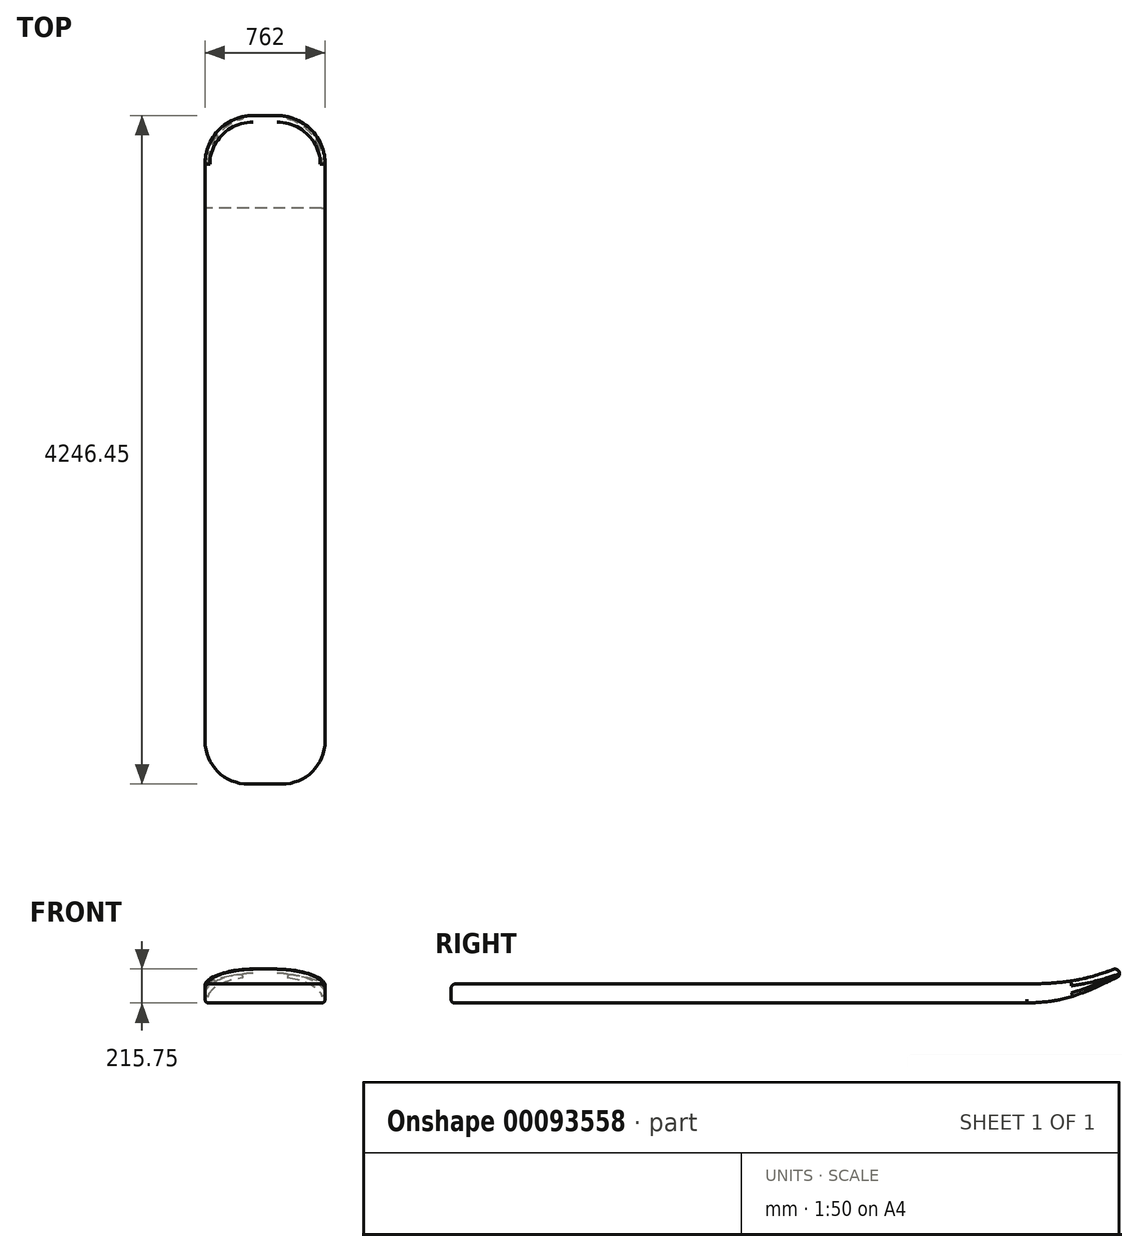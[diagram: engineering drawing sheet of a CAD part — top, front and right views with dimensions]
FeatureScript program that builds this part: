
annotation { "Feature Type Name" : "Feature", "Feature Type Description" : "" }
export const myFeature = defineFeature(function(context is Context, id is Id, definition is map)
    precondition{}
    {
        {
            var Q0;
            Q0=qCreatedBy(makeId("Right.planeOp"),FACE);
            var sketch = newSketch(context, id + "F0", { "sketchPlane" : qUnion([Q0])});
            skLineSegment(sketch, "E0.bottom", {"start": v(0, 0) * mm, "end": v(3657.6, 0) * mm});
            skLineSegment(sketch, "E0.top", {"start": v(0, 121.92) * mm, "end": v(3657.6, 121.92) * mm});
            skLineSegment(sketch, "E0.left", {"start": v(0, 0) * mm, "end": v(0, 121.92) * mm});
            skLineSegment(sketch, "E0.right", {"start": v(3657.6, 0) * mm, "end": v(3657.6, 121.92) * mm, "construction": true});
            skFitSpline(sketch, "E1", {"points": [v(3657.6, 0) * mm, v(3906.08, 30.5) * mm, v(4246.5, 171.9) * mm], "startDerivative": vector(533.96, 24.49) * mm, "endDerivative": vector(640.43, 310.12) * mm});
            skLineSegment(sketch, "E2", {"start": v(4246.5, 171.9) * mm, "end": v(4246.5, 229.2) * mm});
            skFitSpline(sketch, "E3", {"points": [v(4246.5, 229.2) * mm, v(3990.7, 149.5) * mm, v(3657.6, 121.92) * mm], "startDerivative": vector(-520.3, -196.22) * mm, "endDerivative": vector(-655.38, 0) * mm});
            skSolve(sketch);
        }
        {
            var Q0;
            Q0 = qSketchRegion(id + "F0", true);
            extrude(context, id + "F1", {"entities" : qUnion([Q0]), "depth" : 762 * mm, "symmetric" : true});
        }
        {
            var Q0;
            Q0=makeQuery(id+"F1.opExtrude","CAP_EDGE",EDGE,{"disambiguationData":[OSD([sQuery(id+"F0.wireOp",EDGE,"E0.left")])],"isStart":false});
            var Q1;
            Q1=makeQuery(id+"F1.opExtrude","CAP_EDGE",EDGE,{"disambiguationData":[OSD([sQuery(id+"F0.wireOp",EDGE,"E0.left")])],"isStart":true});
            fillet(context, id + "F2", {"entities" : qUnion([Q0, Q1]), "radius" : 274.32 * mm, "tangentPropagation" : true, "allowEdgeOverflow" : false});
        }
        {
            var Q0;
            Q0=makeQuery(id+"F1.opExtrude","CAP_EDGE",EDGE,{"disambiguationData":[OSD([sQuery(id+"F0.wireOp",EDGE,"E2")])],"isStart":false});
            var Q1;
            Q1=makeQuery(id+"F1.opExtrude","CAP_EDGE",EDGE,{"disambiguationData":[OSD([sQuery(id+"F0.wireOp",EDGE,"E2")])],"isStart":true});
            fillet(context, id + "F3", {"entities" : qUnion([Q0, Q1]), "radius" : 304.8 * mm, "tangentPropagation" : true, "allowEdgeOverflow" : false});
        }
        {
            var Q0;
            Q0=makeQuery(id+"F1.opExtrude","CAP_EDGE",EDGE,{"disambiguationData":[OSD([sQuery(id+"F0.wireOp",EDGE,"E0.top")])],"isStart":false});
            var Q1;
            Q1=makeQuery(id+"F1.opExtrude","CAP_EDGE",EDGE,{"disambiguationData":[OSD([sQuery(id+"F0.wireOp",EDGE,"E3")])],"isStart":false});
            var Q2;
            Q2=makeQuery(id+"F3.opFillet","BLEND_EDGE",EDGE,{"blendedFrom":[makeQuery(id+"F1.opExtrude","CAP_EDGE",EDGE,{"disambiguationData":[OSD([sQuery(id+"F0.wireOp",EDGE,"E2")])],"isStart":false}),makeQuery(id+"F1.opExtrude","SWEPT_FACE",FACE,{"disambiguationData":[OSD([sQuery(id+"F0.wireOp",EDGE,"E3")])]})],"blendedInto":[makeQuery(id+"F1.opExtrude","SWEPT_FACE",FACE,{"disambiguationData":[OSD([sQuery(id+"F0.wireOp",EDGE,"E3")])]})]});
            var Q3;
            Q3=makeQuery(id+"F1.opExtrude","SWEPT_EDGE",EDGE,{"disambiguationData":[OSD([sQuery(id+"F0.wireOp",EDGE,"E2"),sQuery(id+"F0.wireOp",EDGE,"E3")])]});
            var Q4;
            Q4=makeQuery(id+"F3.opFillet","BLEND_EDGE",EDGE,{"blendedFrom":[makeQuery(id+"F1.opExtrude","CAP_EDGE",EDGE,{"disambiguationData":[OSD([sQuery(id+"F0.wireOp",EDGE,"E2")])],"isStart":true}),makeQuery(id+"F1.opExtrude","SWEPT_FACE",FACE,{"disambiguationData":[OSD([sQuery(id+"F0.wireOp",EDGE,"E3")])]})],"blendedInto":[makeQuery(id+"F1.opExtrude","SWEPT_FACE",FACE,{"disambiguationData":[OSD([sQuery(id+"F0.wireOp",EDGE,"E3")])]})]});
            var Q5;
            Q5=makeQuery(id+"F1.opExtrude","CAP_EDGE",EDGE,{"disambiguationData":[OSD([sQuery(id+"F0.wireOp",EDGE,"E3")])],"isStart":true});
            var Q6;
            Q6=makeQuery(id+"F1.opExtrude","CAP_EDGE",EDGE,{"disambiguationData":[OSD([sQuery(id+"F0.wireOp",EDGE,"E0.top")])],"isStart":true});
            var Q7;
            Q7=makeQuery(id+"F2.opFillet","BLEND_EDGE",EDGE,{"blendedFrom":[makeQuery(id+"F1.opExtrude","CAP_EDGE",EDGE,{"disambiguationData":[OSD([sQuery(id+"F0.wireOp",EDGE,"E0.left")])],"isStart":true}),makeQuery(id+"F1.opExtrude","SWEPT_FACE",FACE,{"disambiguationData":[OSD([sQuery(id+"F0.wireOp",EDGE,"E0.top")])]})],"blendedInto":[makeQuery(id+"F1.opExtrude","SWEPT_FACE",FACE,{"disambiguationData":[OSD([sQuery(id+"F0.wireOp",EDGE,"E0.top")])]})]});
            var Q8;
            Q8=makeQuery(id+"F1.opExtrude","SWEPT_EDGE",EDGE,{"disambiguationData":[OSD([sQuery(id+"F0.wireOp",EDGE,"E0.top"),sQuery(id+"F0.wireOp",EDGE,"E0.left")])]});
            var Q9;
            Q9=makeQuery(id+"F2.opFillet","BLEND_EDGE",EDGE,{"blendedFrom":[makeQuery(id+"F1.opExtrude","CAP_EDGE",EDGE,{"disambiguationData":[OSD([sQuery(id+"F0.wireOp",EDGE,"E0.left")])],"isStart":false}),makeQuery(id+"F1.opExtrude","SWEPT_FACE",FACE,{"disambiguationData":[OSD([sQuery(id+"F0.wireOp",EDGE,"E0.top")])]})],"blendedInto":[makeQuery(id+"F1.opExtrude","SWEPT_FACE",FACE,{"disambiguationData":[OSD([sQuery(id+"F0.wireOp",EDGE,"E0.top")])]})]});
            fillet(context, id + "F4", {"entities" : qUnion([Q0, Q1, Q2, Q3, Q4, Q5, Q6, Q7, Q8, Q9]), "radius" : 30.48 * mm, "tangentPropagation" : true, "allowEdgeOverflow" : false});
        }
        {
            var Q0;
            Q0=makeQuery(id+"F1.opExtrude","CAP_EDGE",EDGE,{"disambiguationData":[OSD([sQuery(id+"F0.wireOp",EDGE,"E0.bottom")])],"isStart":false});
            var Q1;
            Q1=makeQuery(id+"F3.opFillet","BLEND_EDGE",EDGE,{"blendedFrom":[makeQuery(id+"F1.opExtrude","CAP_EDGE",EDGE,{"disambiguationData":[OSD([sQuery(id+"F0.wireOp",EDGE,"E2")])],"isStart":true}),makeQuery(id+"F1.opExtrude","SWEPT_FACE",FACE,{"disambiguationData":[OSD([sQuery(id+"F0.wireOp",EDGE,"E1")])]})],"blendedInto":[makeQuery(id+"F1.opExtrude","SWEPT_FACE",FACE,{"disambiguationData":[OSD([sQuery(id+"F0.wireOp",EDGE,"E1")])]})]});
            fillet(context, id + "F5", {"entities" : qUnion([Q0, Q1]), "radius" : 22.86 * mm, "tangentPropagation" : true, "allowEdgeOverflow" : false});
        }
    });
